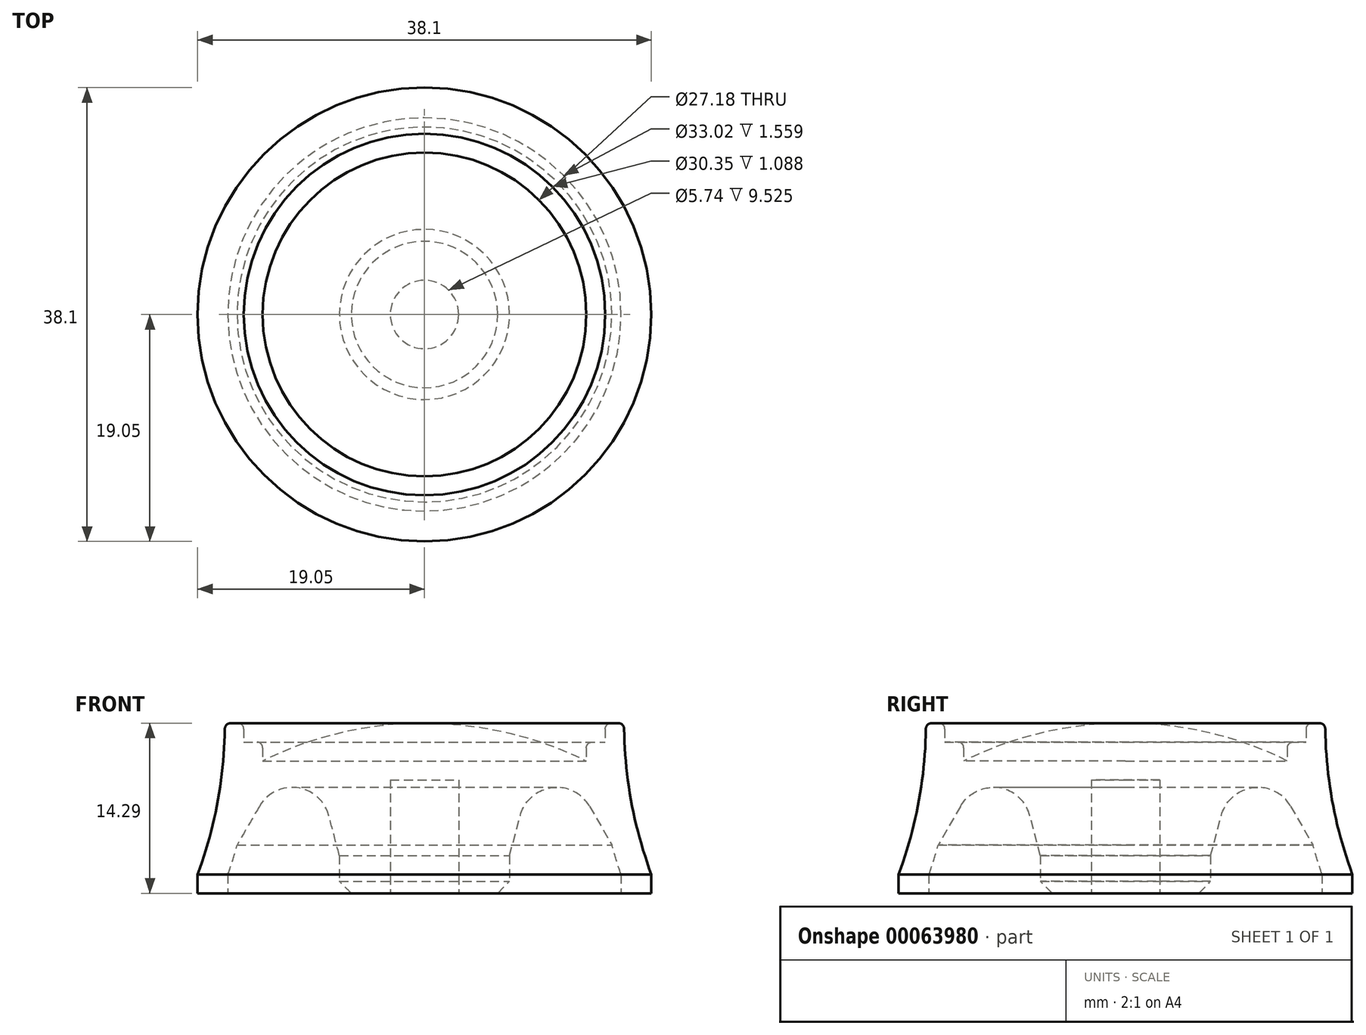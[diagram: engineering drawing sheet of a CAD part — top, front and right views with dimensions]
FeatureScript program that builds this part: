
annotation { "Feature Type Name" : "Feature", "Feature Type Description" : "" }
export const myFeature = defineFeature(function(context is Context, id is Id, definition is map)
    precondition{}
    {
        {
            var Q0;
            Q0=qCreatedBy(makeId("Front.planeOp"),FACE);
            var sketch = newSketch(context, id + "F0", { "sketchPlane" : qUnion([Q0])});
            skLineSegment(sketch, "E0", {"start": v(0, 0) * mm, "end": v(0, 14.29) * mm});
            skLineSegment(sketch, "E1", {"start": v(13.59, 11.11) * mm, "end": v(13.59, 12.7) * mm});
            skLineSegment(sketch, "E2", {"start": v(13.59, 12.7) * mm, "end": v(15.18, 12.7) * mm});
            skLineSegment(sketch, "E3", {"start": v(15.18, 12.7) * mm, "end": v(15.18, 14.29) * mm});
            skLineSegment(sketch, "E4", {"start": v(15.18, 14.29) * mm, "end": v(16.76, 14.29) * mm});
            skArc(sketch, "E5", {"start": v(16.76, 14.29) * mm, "mid": v(17.34, 7.84) * mm, "end": v(19.05, 1.59) * mm});
            skArc(sketch, "E6", {"start": v(13.59, 11.11) * mm, "mid": v(6.98, 13.48) * mm, "end": v(0, 14.29) * mm});
            skLineSegment(sketch, "E7", {"start": v(0, 0) * mm, "end": v(7.14, 0) * mm});
            skLineSegment(sketch, "E8", {"start": v(7.14, 0) * mm, "end": v(7.14, 3.18) * mm});
            skLineSegment(sketch, "E9", {"start": v(19.05, 1.59) * mm, "end": v(19.05, 0) * mm});
            skLineSegment(sketch, "E10", {"start": v(19.05, 0) * mm, "end": v(16.51, 0) * mm});
            skLineSegment(sketch, "E11", {"start": v(16.51, 0) * mm, "end": v(16.51, 1.56) * mm});
            skArc(sketch, "E12", {"start": v(16.5, 1.56) * mm, "mid": v(16.1, 2.8) * mm, "end": v(15.74, 4.05) * mm});
            skLineSegment(sketch, "E13", {"start": v(0, 14.29) * mm, "end": v(0, 33.75) * mm, "construction": true});
            skLineSegment(sketch, "E14", {"start": v(0, 0) * mm, "end": v(0, -16.38) * mm, "construction": true});
            skLineSegment(sketch, "E15", {"start": v(7.14, 3.17) * mm, "end": v(8.04, 6.54) * mm});
            skLineSegment(sketch, "E16", {"start": v(15.74, 4.05) * mm, "end": v(13.86, 7.3) * mm});
            skArc(sketch, "E17", {"start": v(8.04, 6.54) * mm, "mid": v(10.7, 8.86) * mm, "end": v(13.86, 7.3) * mm});
            skSolve(sketch);
        }
        {
            var Q0;
            Q0 = qSketchRegion(id + "F0", true);
            var Q1;
            Q1=sQuery(id+"F0.wireOp",EDGE,"E13");
            revolve(context, id + "F1", {"surfaceOperationType" : NewSurfaceOperationType.NEW, "entities" : qUnion([Q0]), "axis" : qUnion([Q1]), "revolveType" : RevolveType.FULL});
        }
        {
            var Q0;
            Q0=makeQuery(id+"F1.opRevolve","SWEPT_EDGE",EDGE,{"disambiguationData":[OSD([sQuery(id+"F0.wireOp",EDGE,"E4"),sQuery(id+"F0.wireOp",EDGE,"E5")])]});
            var Q1;
            Q1=makeQuery(id+"F1.opRevolve","SWEPT_EDGE",EDGE,{"disambiguationData":[OSD([sQuery(id+"F0.wireOp",EDGE,"E3"),sQuery(id+"F0.wireOp",EDGE,"E4")])]});
            var Q2;
            Q2=makeQuery(id+"F1.opRevolve","SWEPT_EDGE",EDGE,{"disambiguationData":[OSD([sQuery(id+"F0.wireOp",EDGE,"E1"),sQuery(id+"F0.wireOp",EDGE,"E2")])]});
            fillet(context, id + "F2", {"entities" : qUnion([Q0, Q1, Q2]), "radius" : 0.5 * mm, "tangentPropagation" : true, "allowEdgeOverflow" : false});
        }
        {
            var Q0;
            Q0=makeQuery(id+"F1.opRevolve","SWEPT_FACE",FACE,{"disambiguationData":[OSD([sQuery(id+"F0.wireOp",EDGE,"E7")])]});
            var sketch = newSketch(context, id + "F3", { "sketchPlane" : qUnion([Q0])});
            skCircle(sketch, "E18", {"center": v(0, 0) * mm, "radius": 2.87 * mm});
            skSolve(sketch);
        }
        {
            var Q0;
            Q0 = qSketchRegion(id + "F3", true);
            extrude(context, id + "F4", {"entities" : qUnion([Q0]), "operationType" : NewBodyOperationType.REMOVE, "oppositeDirection" : true, "depth" : 9.52 * mm, "offsetDistance" : 25.4 * mm});
        }
        {
            var Q0;
            Q0=makeQuery(id+"F4.boolean.opBoolean","COPY",EDGE,{"derivedFrom":makeQuery(id+"F4.opExtrude","CAP_EDGE",EDGE,{"disambiguationData":[OSD([sQuery(id+"F3.wireOp",EDGE,"E18")])],"isStart":true})});
            var Q1;
            Q1=makeQuery(id+"F1.opRevolve","SWEPT_EDGE",EDGE,{"disambiguationData":[OSD([sQuery(id+"F0.wireOp",EDGE,"E7"),sQuery(id+"F0.wireOp",EDGE,"E8")])]});
            chamfer(context, id + "F5", {"entities" : qUnion([Q0, Q1]), "width" : 1 * mm, "tangentPropagation" : true});
        }
    });
